FCSTD DOCUMENT  (FreeCAD 0.22R36731 (Git))
Label: test
License: All rights reserved
objects: Sketcher::SketchObject×1
note: 1 computed .brp shape members not serialized (recipe doc carries the construction recipe); baked Part::Feature solids carry a one-line shape summary decoded from their .brp

FEATURE [Sketcher::SketchObject] Sketch
  FullyConstrained = false
  sketch-geometry (14):
    g0: ArcOfCircle CenterX=0 CenterY=0 CenterZ=0 NormalX=0 NormalY=0 NormalZ=1 AngleXU=0 Radius=300 StartAngle=1.15648 EndAngle=3.14159
    g1: ArcOfCircle CenterX=600 CenterY=-100 CenterZ=0 NormalX=0 NormalY=0 NormalZ=1 AngleXU=0 Radius=150 StartAngle=1e-16 EndAngle=1.15648
    g2: LineSegment StartX=-300 StartY=3.67e-14 StartZ=0 EndX=-300 EndY=-200 EndZ=0
    g3: LineSegment StartX=-300 StartY=-200 StartZ=0 EndX=750 EndY=-200 EndZ=0
    g4: LineSegment StartX=750 StartY=-100 StartZ=0 EndX=750 EndY=-200 EndZ=0
    g5: LineSegment StartX=660.385 StartY=37.3087 StartZ=0 EndX=120.77 EndY=274.617 EndZ=0
    g6: LineSegment StartX=0 StartY=0 StartZ=0 EndX=120.77 EndY=274.617 EndZ=0
    g7: LineSegment StartX=600 StartY=-100 StartZ=0 EndX=660.385 EndY=37.3087 EndZ=0
    g8: LineSegment StartX=600 StartY=-100 StartZ=0 EndX=600 EndY=35.4144 EndZ=0
    g9: LineSegment StartX=0 StartY=0 StartZ=0 EndX=600 EndY=-100 EndZ=0
    g10: LineSegment StartX=600 StartY=-100 StartZ=0 EndX=750 EndY=-100 EndZ=0
    g11: LineSegment StartX=600 StartY=-100 StartZ=0 EndX=725.614 EndY=-18.0174 EndZ=0
    g12: LineSegment StartX=660.385 StartY=37.3087 StartZ=0 EndX=120.77 EndY=274.617 EndZ=0
    g13: LineSegment StartX=600 StartY=-100 StartZ=0 EndX=60.3848 EndY=137.309 EndZ=0
  constraints (41):
    c: Coincident(g0,g-1)
    c: Vertical(g2)
    c: Coincident(g3,g2)
    c: Horizontal(g3)
    c: Coincident(g4,g3)
    c: Vertical(g4)
    c: Coincident(g0,g2)
    c: Tangent(g1,g4) = 1.5708
    c: Radius(g0) = 300
    c: PointOnObject(g0,g-1)
    c: DistanceX(g0,g1) = 600
    c: Tangent(g0,g5) = -1.5708
    c: Tangent(g1,g5) = -1.5708
    c: DistanceY(g2,g2) = 200
    c: DistanceY(g4,g4) = 100
    c: Coincident(g6,g0)
    c: Coincident(g6,g0)
    c: Coincident(g7,g1)
    c: Coincident(g7,g1)
    c: Angle(g-1,g6) = 1.15648
    c: Coincident(g8,g1)
    c: Vertical(g8)
    c: Angle(g7,g8) = 0.414317
    c: Angle(g6,g-2) = 0.414317
    c: DistanceX(g1,g3) = 150
    c: Coincident(g9,g0)
    c: Coincident(g9,g1)
    c: Coincident(g10,g1)
    c: Coincident(g10,g1)
    c: Coincident(g11,g1)
    c: Angle(g10,g11) = 0.57824
    c: PointOnObject(g11,g1)
    c: DistanceX(g-1,g11) = 725.614
    c: Coincident(g12,g1)
    c: PointOnObject(g12,g6)
    c: Perpendicular(g6,g12)
    c: Coincident(g13,g1)
    c: Symmetric(g6,g6,g13)
    c: Distance(g9,g9) = 608.276
    c: Angle(g13,g9) = 0.249169
    c: Angle(g9,g-1) = 0.165149
